# Revit family: Fluted CMU-4 Flutes-Section
name_source: partatom
category: Detail Items
revit_build: Autodesk Revit Architecture 2012 (Build: 20110210_1515)
units: mm (PartAtom-declared; Revit-internal decimal feet)

## types (13) — shared parameters
Flute Depth = 0' - 1 5/8"
Joint = 0' - 0 3/8"

## per-type parameters (varying)
| type | Core Visibility | Face | Height | Keynote | Length | Thickness | Web |
| 4" x 8" x 8" | Yes | 0' - 0 3/4" | 0' - 7 5/8" | 04 22 00.D2 | 0' - 7 5/8" | 0' - 3 5/8" | 0' - 0 3/4" |
| 2" x 8" x 8" | No | 0' - 0 1/2" | 0' - 7 5/8" | 04 22 00.D1 | 0' - 7 5/8" | 0' - 1 5/8" | 0' - 0 3/4" |
| 6" x 8" x 8" | Yes | 0' - 1" | 0' - 7 5/8" | 04 22 00.D3 | 0' - 7 5/8" | 0' - 5 5/8" | 0' - 1" |
| 8" x 8" x 8" | Yes | 0' - 1 1/4" | 0' - 7 5/8" | 04 22 00.D4 | 0' - 7 5/8" | 0' - 7 5/8" | 0' - 1" |
| 4" x 4" x 16" | Yes | 0' - 0 3/4" | 0' - 3 5/8" | 04 22 00.D10 | 1' - 3 5/8" | 0' - 3 5/8" | 0' - 0 3/4" |
| 6" x 4" x 16" | Yes | 0' - 1" | 0' - 3 5/8" | 04 22 00.D11 | 1' - 3 5/8" | 0' - 5 5/8" | 0' - 1" |
| 8" x 4" x 16" | Yes | 0' - 1 1/4" | 0' - 3 5/8" | 04 22 00.D12 | 1' - 3 5/8" | 0' - 7 5/8" | 0' - 1" |
| 2" x 8" x 16" | No | 0' - 0 1/2" | 0' - 7 5/8" | 04 22 00.D13 | 1' - 3 5/8" | 0' - 1 5/8" | 0' - 0 3/4" |
| 4" x 8" x 16" | Yes | 0' - 0 3/4" | 0' - 7 5/8" | 04 22 00.D14 | 1' - 3 5/8" | 0' - 3 5/8" | 0' - 0 3/4" |
| 6" x 8" x 16" | Yes | 0' - 1" | 0' - 7 5/8" | 04 22 00.D15 | 1' - 3 5/8" | 0' - 5 5/8" | 0' - 1" |
| 8" x 8" x 16" | Yes | 0' - 1 1/4" | 0' - 7 5/8" | 04 22 00.D16 | 1' - 3 5/8" | 0' - 7 5/8" | 0' - 1" |
| 10" x 8" x 16" | Yes | 0' - 1 3/8" | 0' - 7 5/8" | 04 22 00.D17 | 1' - 3 5/8" | 0' - 9 5/8" | 0' - 1 1/8" |
| 12" x 8" x 16" | Yes | 0' - 1 1/2" | 0' - 7 5/8" | 04 22 00.D18 | 1' - 3 5/8" | 0' - 11 5/8" | 0' - 1 1/8" |

## geometry (parser evidence)
native form markers: Sweep x1
no freeform markers — native parametric forms only
